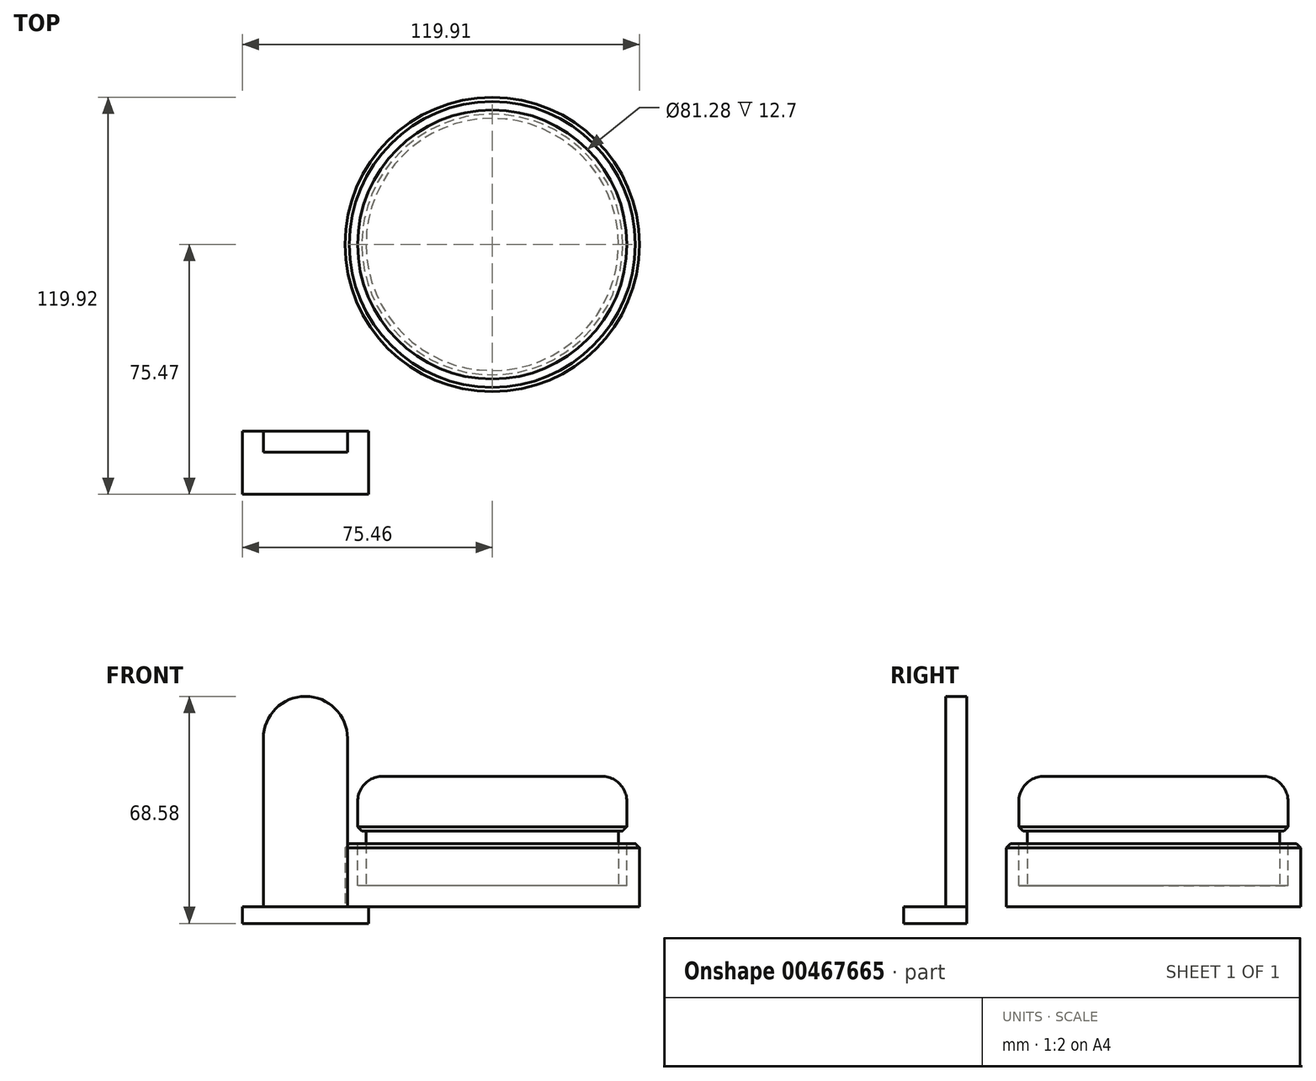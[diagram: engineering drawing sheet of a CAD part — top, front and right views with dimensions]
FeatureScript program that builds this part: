
annotation { "Feature Type Name" : "Feature", "Feature Type Description" : "" }
export const myFeature = defineFeature(function(context is Context, id is Id, definition is map)
    precondition{}
    {
        {
            var Q0;
            Q0=qCreatedBy(makeId("Top.planeOp"),FACE);
            var sketch = newSketch(context, id + "F0", { "sketchPlane" : qUnion([Q0])});
            skCircle(sketch, "E0", {"center": v(0, 0) * mm, "radius": 44.45 * mm});
            skSolve(sketch);
        }
        {
            var Q0;
            Q0 = qSketchRegion(id + "F0", true);
            extrude(context, id + "F1", {"entities" : qUnion([Q0]), "depth" : 19.05 * mm});
        }
        {
            var Q0;
            Q0=makeQuery(id+"F1.opExtrude","CAP_FACE",FACE,{"disambiguationData":[OSD([sQuery(id+"F0.wireOp",EDGE,"E0")])],"isStart":false});
            var sketch = newSketch(context, id + "F2", { "sketchPlane" : qUnion([Q0])});
            skCircle(sketch, "E1", {"center": v(0, 0) * mm, "radius": 40.64 * mm});
            skSolve(sketch);
        }
        {
            var Q0;
            Q0 = qSketchRegion(id + "F2", true);
            extrude(context, id + "F3", {"entities" : qUnion([Q0]), "operationType" : NewBodyOperationType.REMOVE, "oppositeDirection" : true, "depth" : 12.7 * mm});
        }
        {
            var Q0;
            Q0=makeQuery(id+"F3.boolean.opBoolean","COPY",FACE,{"derivedFrom":makeQuery(id+"F3.opExtrude","CAP_FACE",FACE,{"disambiguationData":[OSD([sQuery(id+"F2.wireOp",EDGE,"E1")])],"isStart":false})});
            var sketch = newSketch(context, id + "F4", { "sketchPlane" : qUnion([Q0])});
            skCircle(sketch, "E2", {"center": v(0, 0) * mm, "radius": 38.1 * mm});
            skSolve(sketch);
        }
        {
            var Q0;
            Q0 = qSketchRegion(id + "F4", true);
            extrude(context, id + "F5", {"entities" : qUnion([Q0]), "depth" : 16.5 * mm});
        }
        {
            var Q0;
            Q0=makeQuery(id+"F5.opExtrude","CAP_FACE",FACE,{"disambiguationData":[OSD([sQuery(id+"F4.wireOp",EDGE,"E2")])],"isStart":false});
            var sketch = newSketch(context, id + "F6", { "sketchPlane" : qUnion([Q0])});
            skCircle(sketch, "E3", {"center": v(0, 0) * mm, "radius": 40.64 * mm});
            skSolve(sketch);
        }
        {
            var Q0;
            Q0 = qSketchRegion(id + "F6", true);
            extrude(context, id + "F7", {"entities" : qUnion([Q0]), "operationType" : NewBodyOperationType.ADD, "depth" : 16.5 * mm});
        }
        {
            var Q0;
            Q0=makeQuery(id+"F7.opExtrude","CAP_EDGE",EDGE,{"disambiguationData":[OSD([sQuery(id+"F6.wireOp",EDGE,"E3")])],"isStart":false});
            fillet(context, id + "F8", {"entities" : qUnion([Q0]), "radius" : 7.62 * mm, "tangentPropagation" : true, "allowEdgeOverflow" : false});
        }
        {
            var Q0;
            Q0=makeQuery(id+"F1.opExtrude","CAP_EDGE",EDGE,{"disambiguationData":[OSD([sQuery(id+"F0.wireOp",EDGE,"E0")])],"isStart":false});
            var Q1;
            Q1=makeQuery(id+"F7.opExtrude","CAP_EDGE",EDGE,{"disambiguationData":[OSD([sQuery(id+"F6.wireOp",EDGE,"E3")])],"isStart":true});
            chamfer(context, id + "F9", {"entities" : qUnion([Q0, Q1]), "width" : 1.27 * mm, "tangentPropagation" : true});
        }
        {
            var Q0;
            Q0=qCreatedBy(makeId("Top.planeOp"),FACE);
            var sketch = newSketch(context, id + "F10", { "sketchPlane" : qUnion([Q0])});
            skLineSegment(sketch, "E4.bottom", {"start": v(-75.46, -56.42) * mm, "end": v(-37.36, -56.42) * mm});
            skLineSegment(sketch, "E4.top", {"start": v(-75.46, -75.47) * mm, "end": v(-37.36, -75.47) * mm});
            skLineSegment(sketch, "E4.left", {"start": v(-75.46, -56.42) * mm, "end": v(-75.46, -75.47) * mm});
            skLineSegment(sketch, "E4.right", {"start": v(-37.36, -56.42) * mm, "end": v(-37.36, -75.47) * mm});
            skSolve(sketch);
        }
        {
            var Q0;
            Q0 = qSketchRegion(id + "F10", true);
            extrude(context, id + "F11", {"entities" : qUnion([Q0]), "oppositeDirection" : true, "depth" : 5.08 * mm});
        }
        {
            var Q0;
            Q0=makeQuery(id+"F11.opExtrude","CAP_FACE",FACE,{"disambiguationData":[OSD([sQuery(id+"F10.wireOp",EDGE,"E4.bottom"),sQuery(id+"F10.wireOp",EDGE,"E4.top"),sQuery(id+"F10.wireOp",EDGE,"E4.left"),sQuery(id+"F10.wireOp",EDGE,"E4.right")])],"isStart":true});
            var sketch = newSketch(context, id + "F12", { "sketchPlane" : qUnion([Q0])});
            skLineSegment(sketch, "E5.bottom", {"start": v(-69.11, -56.42) * mm, "end": v(-43.71, -56.42) * mm});
            skLineSegment(sketch, "E5.top", {"start": v(-69.11, -62.77) * mm, "end": v(-43.71, -62.77) * mm});
            skLineSegment(sketch, "E5.left", {"start": v(-69.11, -56.42) * mm, "end": v(-69.11, -62.77) * mm});
            skLineSegment(sketch, "E5.right", {"start": v(-43.71, -56.42) * mm, "end": v(-43.71, -62.77) * mm});
            skSolve(sketch);
        }
        {
            var Q0;
            Q0 = qSketchRegion(id + "F12", true);
            extrude(context, id + "F13", {"entities" : qUnion([Q0]), "operationType" : NewBodyOperationType.ADD, "depth" : 50.8 * mm});
        }
        {
            var Q0;
            Q0=makeQuery(id+"F13.opExtrude","SWEPT_FACE",FACE,{"disambiguationData":[OSD([sQuery(id+"F12.wireOp",EDGE,"E5.top")])]});
            var sketch = newSketch(context, id + "F14", { "sketchPlane" : qUnion([Q0])});
            skArc(sketch, "E6", {"start": v(-43.71, 50.8) * mm, "mid": v(-56.41, 63.5) * mm, "end": v(-69.11, 50.8) * mm});
            skLineSegment(sketch, "E7", {"start": v(-69.11, 50.8) * mm, "end": v(-43.71, 50.8) * mm});
            skSolve(sketch);
        }
        {
            var Q0;
            Q0 = qSketchRegion(id + "F14", true);
            extrude(context, id + "F15", {"entities" : qUnion([Q0]), "operationType" : NewBodyOperationType.ADD, "oppositeDirection" : true, "depth" : 6.35 * mm});
        }
    });
